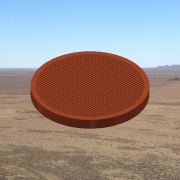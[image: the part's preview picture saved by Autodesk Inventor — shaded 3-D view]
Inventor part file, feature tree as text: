
AUTODESK INVENTOR PART (.ipt)
format: ipt  version: 2014 SP1 (Build 180222100, 222)  size: 3,876,864 bytes
history: native  units: in
note: dims shown in document units (in); Inventor stores cm internally (conversion verified against a paired STEP export)
features: sketch x2, extrude x1, other x1
ambient origin geometry x8: Origin, YZ Plane, XZ Plane, XY Plane, X Axis, Y Axis, Z Axis, Center Point
bodies: Solid1 (feature_tree)
feature tree (4):
  extrude  "Extrusion1"  Depth=1.0in TaperAngle=0.0deg
  other  "Grill4"
  sketch  "Sketch1"  dims[d0=11.0in d1=1.0in d2=0.0in]
  sketch  "Sketch5"  dims[d78=0.5in d79=8.2677in d81=0.25in d82=8.2677in d84=0.25in d87=8.2677in d89=0.25in d90=8.2677in d92=0.25in d95=0.1in d96=1.0in d97=0.0in d98=0.1in d99=1.0in d100=0.0in d101=0.1in d102=0.0in d103=0.0in d104=0.05in d105=0.0in d106=0.0in d107=0.0in d108=71.9605in]
